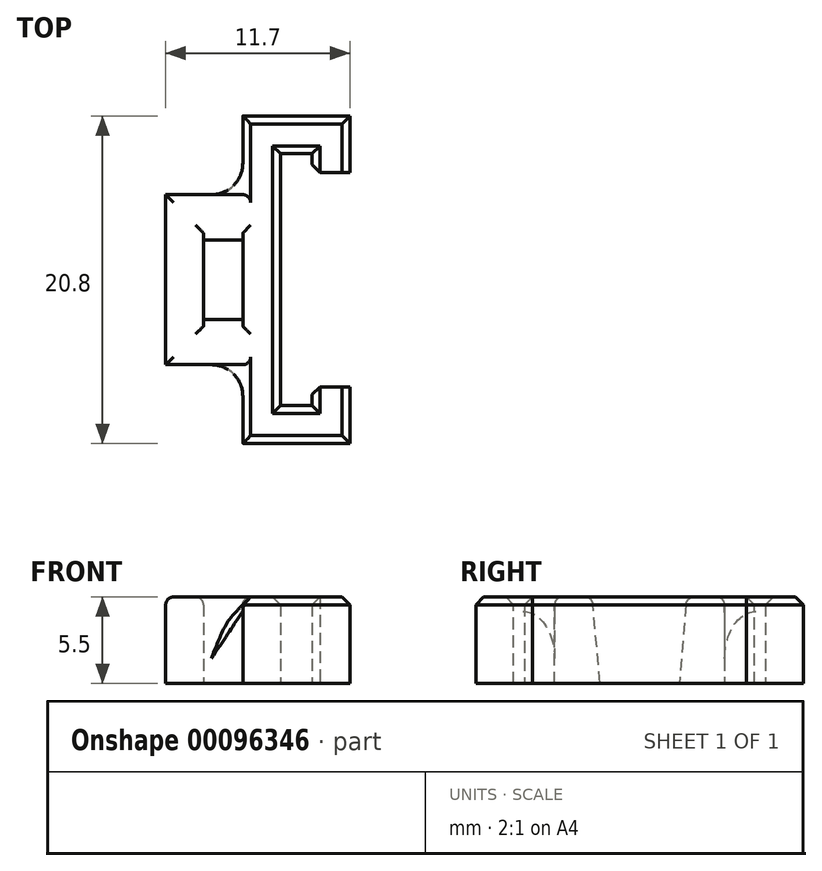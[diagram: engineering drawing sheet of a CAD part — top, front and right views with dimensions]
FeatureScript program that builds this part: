
annotation { "Feature Type Name" : "Feature", "Feature Type Description" : "" }
export const myFeature = defineFeature(function(context is Context, id is Id, definition is map)
    precondition{}
    {
        {
            var Q0;
            Q0=qCreatedBy(makeId("Top.planeOp"),FACE);
            var sketch = newSketch(context, id + "F0", { "sketchPlane" : qUnion([Q0])});
            skLineSegment(sketch, "E0", {"start": v(0, 3) * mm, "end": v(0, 0) * mm});
            skLineSegment(sketch, "E1", {"start": v(0, 5.4) * mm, "end": v(0, 10.4) * mm});
            skLineSegment(sketch, "E2", {"start": v(0, 10.4) * mm, "end": v(6.8, 10.4) * mm});
            skLineSegment(sketch, "E3", {"start": v(4.4, 8) * mm, "end": v(2.4, 8) * mm});
            skLineSegment(sketch, "E4", {"start": v(2.4, 8) * mm, "end": v(2.4, 0) * mm});
            skLineSegment(sketch, "E5", {"start": v(6.8, 10.4) * mm, "end": v(6.8, 6.8) * mm});
            skLineSegment(sketch, "E6", {"start": v(6.8, 6.8) * mm, "end": v(4.4, 6.8) * mm});
            skLineSegment(sketch, "E7", {"start": v(4.4, 6.8) * mm, "end": v(4.4, 8) * mm});
            skPoint(sketch, "E8.end.orphan", {"position": v(17.25, 8) * mm});
            skLineSegment(sketch, "E9", {"start": v(0, 5.4) * mm, "end": v(-4.9, 5.4) * mm});
            skLineSegment(sketch, "E10", {"start": v(-4.9, 5.4) * mm, "end": v(-4.9, 0) * mm});
            skLineSegment(sketch, "E11", {"start": v(-2.5, 0) * mm, "end": v(-2.5, 3) * mm});
            skLineSegment(sketch, "E12", {"start": v(-2.5, 3) * mm, "end": v(0, 3) * mm});
            skLineSegment(sketch, "E13", {"start": v(-14.12, 0) * mm, "end": v(-2.5, 0) * mm});
            skPoint(sketch, "E14.start.orphan", {"position": v(0, -10.2) * mm});
            skPoint(sketch, "E15.end.orphan", {"position": v(0, -11.4) * mm});
            skPoint(sketch, "E16.end.orphan", {"position": v(0, -45.73) * mm});
            skPoint(sketch, "E17.end.orphan", {"position": v(17.05, -44.53) * mm});
            skPoint(sketch, "E18.start.orphan", {"position": v(6.8, -45.73) * mm});
            skPoint(sketch, "E19.end.orphan", {"position": v(17.05, -37.9) * mm});
            skLineSegment(sketch, "E20.trimOffspring", {"start": v(0, 0) * mm, "end": v(14.97, 0) * mm});
            skSolve(sketch);
        }
        {
            var Q0;
            Q0=qSketchRegion(id+"F0",true);
            extrude(context, id + "F1", {"entities" : qUnion([Q0]), "depth" : 5.5 * mm});
        }
        {
            var Q0;
            Q0=makeQuery(id+"F1.opExtrude","SWEPT_FACE",FACE,{"disambiguationData":[OSD([sQuery(id+"F0.wireOp",EDGE,"E13")])]});
            var sketch = newSketch(context, id + "F2", { "sketchPlane" : qUnion([Q0])});
            skLineSegment(sketch, "E21", {"start": v(-4.9, 2.75) * mm, "end": v(6.57, 2.75) * mm});
            skSolve(sketch);
        }
        {
            var Q0;
            Q0=makeQuery(id+"F1.opExtrude","SWEPT_BODY",BODY,{"disambiguationData":[OSD([sQuery(id+"F0.wireOp",EDGE,"E0"),sQuery(id+"F0.wireOp",EDGE,"E1"),sQuery(id+"F0.wireOp",EDGE,"E2"),sQuery(id+"F0.wireOp",EDGE,"E3"),sQuery(id+"F0.wireOp",EDGE,"E4"),sQuery(id+"F0.wireOp",EDGE,"E5"),sQuery(id+"F0.wireOp",EDGE,"E6"),sQuery(id+"F0.wireOp",EDGE,"E7"),sQuery(id+"F0.wireOp",EDGE,"E9"),sQuery(id+"F0.wireOp",EDGE,"E10"),sQuery(id+"F0.wireOp",EDGE,"E11"),sQuery(id+"F0.wireOp",EDGE,"E12"),sQuery(id+"F0.wireOp",EDGE,"E13"),sQuery(id+"F0.wireOp",EDGE,"E20.trimOffspring")])]});
            var Q1;
            Q1=sQuery(id+"F2.wireOp",EDGE,"E21");
            circularPattern(context, id + "F3", {"entities" : qUnion([Q0]), "axis" : qUnion([Q1]), "angle" : 180 * degree, "instanceCount" : 2});
        }
        {
            var Q0;
            Q0=makeQuery(id+"F1.opExtrude","SWEPT_BODY",BODY,{"disambiguationData":[OSD([sQuery(id+"F0.wireOp",EDGE,"E0"),sQuery(id+"F0.wireOp",EDGE,"E1"),sQuery(id+"F0.wireOp",EDGE,"E2"),sQuery(id+"F0.wireOp",EDGE,"E3"),sQuery(id+"F0.wireOp",EDGE,"E4"),sQuery(id+"F0.wireOp",EDGE,"E5"),sQuery(id+"F0.wireOp",EDGE,"E6"),sQuery(id+"F0.wireOp",EDGE,"E7"),sQuery(id+"F0.wireOp",EDGE,"E9"),sQuery(id+"F0.wireOp",EDGE,"E10"),sQuery(id+"F0.wireOp",EDGE,"E11"),sQuery(id+"F0.wireOp",EDGE,"E12"),sQuery(id+"F0.wireOp",EDGE,"E13"),sQuery(id+"F0.wireOp",EDGE,"E20.trimOffspring")])]});
            var Q1;
            Q1=makeQuery(id+"F3.opPattern","COPY",BODY,{"derivedFrom":makeQuery(id+"F1.opExtrude","SWEPT_BODY",BODY,{"disambiguationData":[OSD([sQuery(id+"F0.wireOp",EDGE,"E0"),sQuery(id+"F0.wireOp",EDGE,"E1"),sQuery(id+"F0.wireOp",EDGE,"E2"),sQuery(id+"F0.wireOp",EDGE,"E3"),sQuery(id+"F0.wireOp",EDGE,"E4"),sQuery(id+"F0.wireOp",EDGE,"E5"),sQuery(id+"F0.wireOp",EDGE,"E6"),sQuery(id+"F0.wireOp",EDGE,"E7"),sQuery(id+"F0.wireOp",EDGE,"E9"),sQuery(id+"F0.wireOp",EDGE,"E10"),sQuery(id+"F0.wireOp",EDGE,"E11"),sQuery(id+"F0.wireOp",EDGE,"E12"),sQuery(id+"F0.wireOp",EDGE,"E13"),sQuery(id+"F0.wireOp",EDGE,"E20.trimOffspring")])]}),"instanceName":"1"});
            booleanBodies(context, id + "F4", {"operationType" : BooleanOperationType.UNION, "tools" : qUnion([Q0, Q1])});
        }
        {
            var Q0;
            Q0=makeQuery(id+"F3.opPattern","COPY",FACE,{"derivedFrom":makeQuery(id+"F1.opExtrude","SWEPT_FACE",FACE,{"disambiguationData":[OSD([sQuery(id+"F0.wireOp",EDGE,"E12")])]}),"instanceName":"1"});
            var Q1;
            Q1=makeQuery(id+"F3.opPattern","COPY",EDGE,{"derivedFrom":makeQuery(id+"F1.opExtrude","CAP_EDGE",EDGE,{"disambiguationData":[OSD([sQuery(id+"F0.wireOp",EDGE,"E12")])],"isStart":true}),"instanceName":"1"});
            revolve(context, id + "F5", {"operationType" : NewBodyOperationType.ADD, "entities" : qUnion([Q0]), "axis" : qUnion([Q1]), "revolveType" : RevolveType.ONE_DIRECTION, "angle" : 5 * degree});
        }
        {
            var Q0;
            Q0=makeQuery(id+"F1.opExtrude","SWEPT_FACE",FACE,{"disambiguationData":[OSD([sQuery(id+"F0.wireOp",EDGE,"E12")])]});
            var Q1;
            Q1=makeQuery(id+"F1.opExtrude","CAP_EDGE",EDGE,{"disambiguationData":[OSD([sQuery(id+"F0.wireOp",EDGE,"E12")])],"isStart":false});
            revolve(context, id + "F6", {"operationType" : NewBodyOperationType.ADD, "entities" : qUnion([Q0]), "axis" : qUnion([Q1]), "revolveType" : RevolveType.ONE_DIRECTION, "oppositeDirection" : true, "angle" : 5 * degree});
        }
        {
            var Q0;
            {var subQ0=sQuery(id+"F0.wireOp",EDGE,"E12");var subQ1=makeQuery(id+"F1.opExtrude","CAP_EDGE",EDGE,{"disambiguationData":[OSD([subQ0])],"isStart":false});Q0=makeQuery(id+"F6.boolean.opBoolean","MERGE",EDGE,{"derivedFrom":[subQ1,makeQuery(id+"F6.opRevolve","CAP_EDGE",EDGE,{"disambiguationData":[OSD([subQ0]),TDD([subQ1])],"isStart":true})]});}
            var Q1;
            {var subQ0=sQuery(id+"F0.wireOp",EDGE,"E12");var subQ1=makeQuery(id+"F3.opPattern","COPY",EDGE,{"derivedFrom":makeQuery(id+"F1.opExtrude","CAP_EDGE",EDGE,{"disambiguationData":[OSD([subQ0])],"isStart":true}),"instanceName":"1"});Q1=makeQuery(id+"F5.boolean.opBoolean","MERGE",EDGE,{"derivedFrom":[subQ1,makeQuery(id+"F5.opRevolve","CAP_EDGE",EDGE,{"disambiguationData":[OSD([subQ0]),TDD([subQ1])],"isStart":true})]});}
            var Q2;
            {var subQ0=sQuery(id+"F0.wireOp",EDGE,"E0");Q2=makeQuery(id+"F4.opBoolean","MERGE",EDGE,{"derivedFrom":[makeQuery(id+"F1.opExtrude","CAP_EDGE",EDGE,{"disambiguationData":[OSD([subQ0])],"isStart":false}),makeQuery(id+"F3.opPattern","COPY",EDGE,{"derivedFrom":makeQuery(id+"F1.opExtrude","CAP_EDGE",EDGE,{"disambiguationData":[OSD([subQ0])],"isStart":true}),"instanceName":"1"})]});}
            var Q3;
            {var subQ0=sQuery(id+"F0.wireOp",EDGE,"E11");Q3=makeQuery(id+"F4.opBoolean","MERGE",EDGE,{"derivedFrom":[makeQuery(id+"F1.opExtrude","CAP_EDGE",EDGE,{"disambiguationData":[OSD([subQ0])],"isStart":false}),makeQuery(id+"F3.opPattern","COPY",EDGE,{"derivedFrom":makeQuery(id+"F1.opExtrude","CAP_EDGE",EDGE,{"disambiguationData":[OSD([subQ0])],"isStart":true}),"instanceName":"1"})]});}
            var Q4;
            Q4=makeQuery(id+"F3.opPattern","COPY",EDGE,{"derivedFrom":makeQuery(id+"F1.opExtrude","CAP_EDGE",EDGE,{"disambiguationData":[OSD([sQuery(id+"F0.wireOp",EDGE,"E9")])],"isStart":true}),"instanceName":"1"});
            var Q5;
            {var subQ0=sQuery(id+"F0.wireOp",EDGE,"E10");Q5=makeQuery(id+"F4.opBoolean","MERGE",EDGE,{"derivedFrom":[makeQuery(id+"F1.opExtrude","CAP_EDGE",EDGE,{"disambiguationData":[OSD([subQ0])],"isStart":false}),makeQuery(id+"F3.opPattern","COPY",EDGE,{"derivedFrom":makeQuery(id+"F1.opExtrude","CAP_EDGE",EDGE,{"disambiguationData":[OSD([subQ0])],"isStart":true}),"instanceName":"1"})]});}
            var Q6;
            Q6=makeQuery(id+"F1.opExtrude","CAP_EDGE",EDGE,{"disambiguationData":[OSD([sQuery(id+"F0.wireOp",EDGE,"E9")])],"isStart":false});
            fillet(context, id + "F7", {"entities" : qUnion([Q0, Q1, Q2, Q3, Q4, Q5, Q6]), "radius" : .5 * mm, "tangentPropagation" : true, "allowEdgeOverflow" : false});
        }
        {
            var Q0;
            Q0=makeQuery(id+"F3.opPattern","COPY",EDGE,{"derivedFrom":makeQuery(id+"F1.opExtrude","CAP_EDGE",EDGE,{"disambiguationData":[OSD([sQuery(id+"F0.wireOp",EDGE,"E7")])],"isStart":true}),"instanceName":"1"});
            var Q1;
            Q1=makeQuery(id+"F1.opExtrude","CAP_EDGE",EDGE,{"disambiguationData":[OSD([sQuery(id+"F0.wireOp",EDGE,"E7")])],"isStart":false});
            var Q2;
            {var subQ0=sQuery(id+"F0.wireOp",EDGE,"E4");Q2=makeQuery(id+"F4.opBoolean","MERGE",EDGE,{"derivedFrom":[makeQuery(id+"F1.opExtrude","CAP_EDGE",EDGE,{"disambiguationData":[OSD([subQ0])],"isStart":false}),makeQuery(id+"F3.opPattern","COPY",EDGE,{"derivedFrom":makeQuery(id+"F1.opExtrude","CAP_EDGE",EDGE,{"disambiguationData":[OSD([subQ0])],"isStart":true}),"instanceName":"1"})]});}
            var Q3;
            Q3=makeQuery(id+"F1.opExtrude","CAP_EDGE",EDGE,{"disambiguationData":[OSD([sQuery(id+"F0.wireOp",EDGE,"E3")])],"isStart":false});
            var Q4;
            Q4=makeQuery(id+"F3.opPattern","COPY",EDGE,{"derivedFrom":makeQuery(id+"F1.opExtrude","CAP_EDGE",EDGE,{"disambiguationData":[OSD([sQuery(id+"F0.wireOp",EDGE,"E3")])],"isStart":true}),"instanceName":"1"});
            var Q5;
            Q5=makeQuery(id+"F1.opExtrude","CAP_EDGE",EDGE,{"disambiguationData":[OSD([sQuery(id+"F0.wireOp",EDGE,"E5")])],"isStart":false});
            var Q6;
            Q6=makeQuery(id+"F1.opExtrude","CAP_EDGE",EDGE,{"disambiguationData":[OSD([sQuery(id+"F0.wireOp",EDGE,"E2")])],"isStart":false});
            var Q7;
            Q7=makeQuery(id+"F1.opExtrude","CAP_EDGE",EDGE,{"disambiguationData":[OSD([sQuery(id+"F0.wireOp",EDGE,"E1")])],"isStart":false});
            var Q8;
            Q8=makeQuery(id+"F3.opPattern","COPY",EDGE,{"derivedFrom":makeQuery(id+"F1.opExtrude","CAP_EDGE",EDGE,{"disambiguationData":[OSD([sQuery(id+"F0.wireOp",EDGE,"E1")])],"isStart":true}),"instanceName":"1"});
            var Q9;
            Q9=makeQuery(id+"F3.opPattern","COPY",EDGE,{"derivedFrom":makeQuery(id+"F1.opExtrude","CAP_EDGE",EDGE,{"disambiguationData":[OSD([sQuery(id+"F0.wireOp",EDGE,"E2")])],"isStart":true}),"instanceName":"1"});
            var Q10;
            Q10=makeQuery(id+"F3.opPattern","COPY",EDGE,{"derivedFrom":makeQuery(id+"F1.opExtrude","CAP_EDGE",EDGE,{"disambiguationData":[OSD([sQuery(id+"F0.wireOp",EDGE,"E5")])],"isStart":true}),"instanceName":"1"});
            var Q11;
            Q11=makeQuery(id+"F1.opExtrude","SWEPT_EDGE",EDGE,{"disambiguationData":[OSD([sQuery(id+"F0.wireOp",EDGE,"E6"),sQuery(id+"F0.wireOp",EDGE,"E7")])]});
            var Q12;
            Q12=makeQuery(id+"F3.opPattern","COPY",EDGE,{"derivedFrom":makeQuery(id+"F1.opExtrude","SWEPT_EDGE",EDGE,{"disambiguationData":[OSD([sQuery(id+"F0.wireOp",EDGE,"E6"),sQuery(id+"F0.wireOp",EDGE,"E7")])]}),"instanceName":"1"});
            chamfer(context, id + "F8", {"entities" : qUnion([Q0, Q1, Q2, Q3, Q4, Q5, Q6, Q7, Q8, Q9, Q10, Q11, Q12]), "width" : .5 * mm, "tangentPropagation" : true});
        }
        {
            var Q0;
            Q0=makeQuery(id+"F3.opPattern","COPY",EDGE,{"derivedFrom":makeQuery(id+"F1.opExtrude","SWEPT_EDGE",EDGE,{"disambiguationData":[OSD([sQuery(id+"F0.wireOp",EDGE,"E1"),sQuery(id+"F0.wireOp",EDGE,"E9")])]}),"instanceName":"1"});
            var Q1;
            Q1=makeQuery(id+"F1.opExtrude","SWEPT_EDGE",EDGE,{"disambiguationData":[OSD([sQuery(id+"F0.wireOp",EDGE,"E1"),sQuery(id+"F0.wireOp",EDGE,"E9")])]});
            fillet(context, id + "F9", {"entities" : qUnion([Q0, Q1]), "radius" : 2 * mm, "tangentPropagation" : true, "allowEdgeOverflow" : false});
        }
        {
            var Q0;
            {var subQ0=sQuery(id+"F0.wireOp",EDGE,"E1");Q0=makeQuery(id+"F9.opFillet","BLEND_EDGE",EDGE,{"blendedFrom":[makeQuery(id+"F3.opPattern","COPY",EDGE,{"derivedFrom":makeQuery(id+"F1.opExtrude","SWEPT_EDGE",EDGE,{"disambiguationData":[OSD([subQ0,sQuery(id+"F0.wireOp",EDGE,"E9")])]}),"instanceName":"1"}),makeQuery(id+"F8.opChamfer","BLEND_FACE",FACE,{"disambiguationData":[OSD([subQ0]),TDD([makeQuery(id+"F3.opPattern","COPY",EDGE,{"derivedFrom":makeQuery(id+"F1.opExtrude","CAP_EDGE",EDGE,{"disambiguationData":[OSD([subQ0])],"isStart":true}),"instanceName":"1"})])]})],"blendedInto":[makeQuery(id+"F8.opChamfer","BLEND_FACE",FACE,{"disambiguationData":[OSD([subQ0]),TDD([makeQuery(id+"F3.opPattern","COPY",EDGE,{"derivedFrom":makeQuery(id+"F1.opExtrude","CAP_EDGE",EDGE,{"disambiguationData":[OSD([subQ0])],"isStart":true}),"instanceName":"1"})])]})]});}
            var Q1;
            {var subQ0=sQuery(id+"F0.wireOp",EDGE,"E1");Q1=makeQuery(id+"F9.opFillet","BLEND_EDGE",EDGE,{"blendedFrom":[makeQuery(id+"F1.opExtrude","SWEPT_EDGE",EDGE,{"disambiguationData":[OSD([subQ0,sQuery(id+"F0.wireOp",EDGE,"E9")])]}),makeQuery(id+"F8.opChamfer","BLEND_FACE",FACE,{"disambiguationData":[OSD([subQ0]),TDD([makeQuery(id+"F1.opExtrude","CAP_EDGE",EDGE,{"disambiguationData":[OSD([subQ0])],"isStart":false})])]})],"blendedInto":[makeQuery(id+"F8.opChamfer","BLEND_FACE",FACE,{"disambiguationData":[OSD([subQ0]),TDD([makeQuery(id+"F1.opExtrude","CAP_EDGE",EDGE,{"disambiguationData":[OSD([subQ0])],"isStart":false})])]})]});}
            fillet(context, id + "F10", {"entities" : qUnion([Q0, Q1]), "radius" : 1 * mm, "tangentPropagation" : true, "allowEdgeOverflow" : false});
        }
    });
